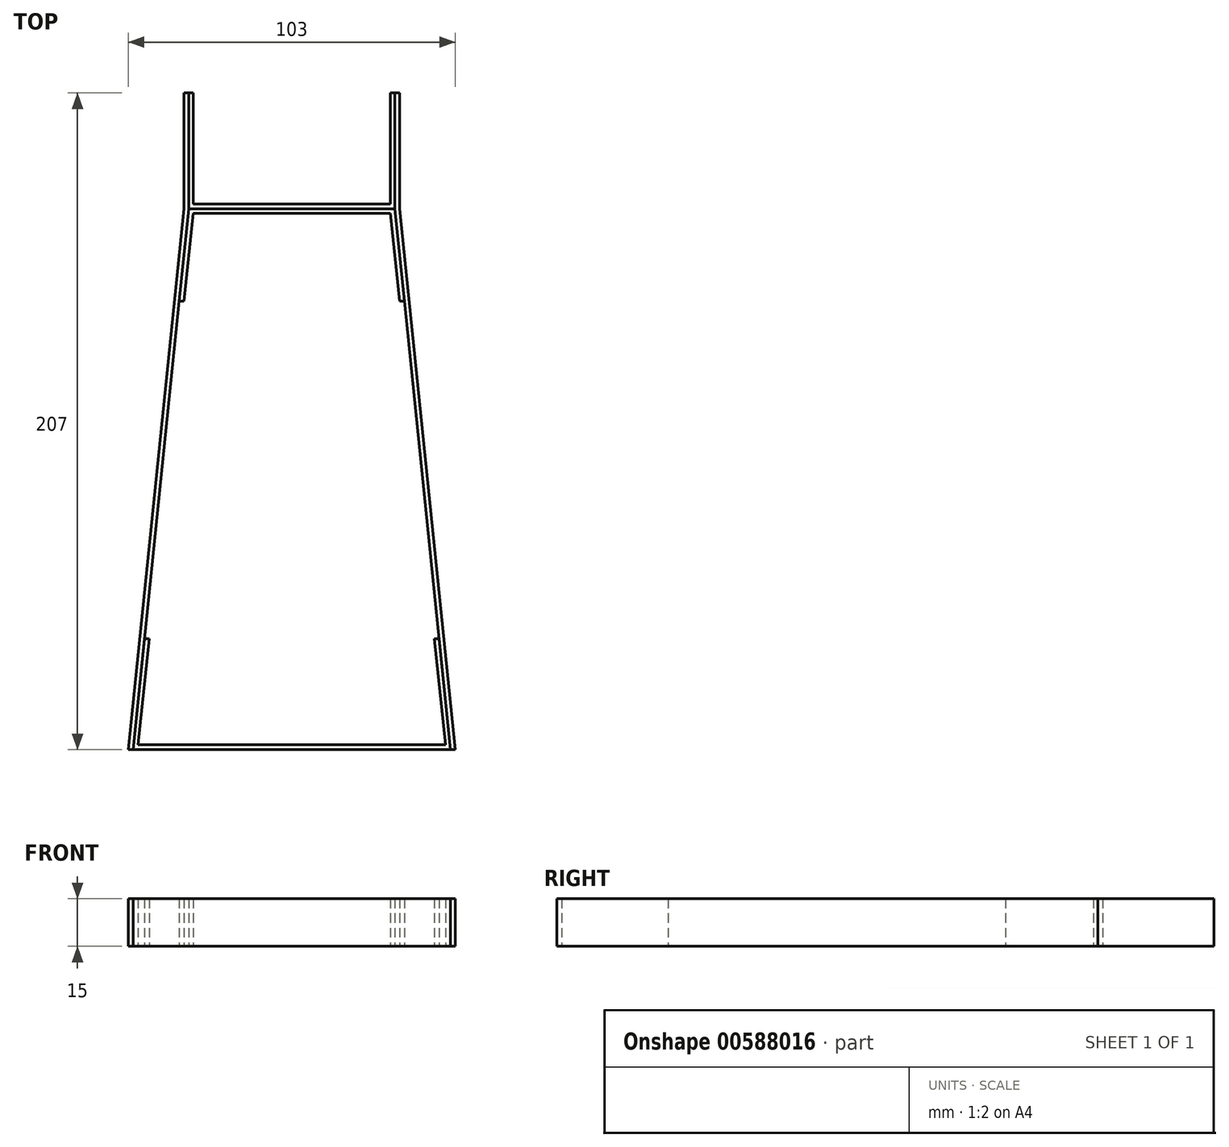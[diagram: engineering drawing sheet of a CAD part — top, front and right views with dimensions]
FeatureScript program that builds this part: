
annotation { "Feature Type Name" : "Feature", "Feature Type Description" : "" }
export const myFeature = defineFeature(function(context is Context, id is Id, definition is map)
    precondition{}
    {
        {
            var Q0;
            Q0=qCreatedBy(makeId("Top.planeOp"),FACE);
            var sketch = newSketch(context, id + "F0", { "sketchPlane" : qUnion([Q0])});
            skLineSegment(sketch, "E0", {"start": v(0, 0) * mm, "end": v(-32.5, 0) * mm});
            skLineSegment(sketch, "E1", {"start": v(-32.5, 0) * mm, "end": v(-32.5, 36.5) * mm});
            skLineSegment(sketch, "E2", {"start": v(-32.5, 36.5) * mm, "end": v(-31, 36.5) * mm});
            skLineSegment(sketch, "E3", {"start": v(-31, 36.5) * mm, "end": v(-31, 1.5) * mm});
            skLineSegment(sketch, "E4", {"start": v(-31, 1.5) * mm, "end": v(0, 1.5) * mm});
            skLineSegment(sketch, "E5.MirrorCS", {"start": v(32.5, 36.5) * mm, "end": v(31, 36.5) * mm});
            skLineSegment(sketch, "E6.MirrorCS", {"start": v(0, 0) * mm, "end": v(32.5, 0) * mm});
            skLineSegment(sketch, "E7.MirrorCS", {"start": v(31, 1.5) * mm, "end": v(0, 1.5) * mm});
            skLineSegment(sketch, "E8.MirrorCS", {"start": v(31, 36.5) * mm, "end": v(31, 1.5) * mm});
            skLineSegment(sketch, "E9.MirrorCS", {"start": v(32.5, 0) * mm, "end": v(32.5, 36.5) * mm});
            skLineSegment(sketch, "E10", {"start": v(-32.5, 0) * mm, "end": v(-35.5, -29.13) * mm});
            skLineSegment(sketch, "E11", {"start": v(-35.5, -29.13) * mm, "end": v(-34, -29.13) * mm});
            skLineSegment(sketch, "E12", {"start": v(-34, -29.13) * mm, "end": v(-31, -1.5) * mm});
            skLineSegment(sketch, "E13", {"start": v(-31, -1.5) * mm, "end": v(0, -1.5) * mm});
            skLineSegment(sketch, "E14.MirrorCS", {"start": v(35.5, -29.13) * mm, "end": v(34, -29.13) * mm});
            skLineSegment(sketch, "E15.MirrorCS", {"start": v(31, -1.5) * mm, "end": v(0, -1.5) * mm});
            skLineSegment(sketch, "E16.MirrorCS", {"start": v(34, -29.13) * mm, "end": v(31, -1.5) * mm});
            skLineSegment(sketch, "E17.MirrorCS", {"start": v(32.5, 0) * mm, "end": v(35.5, -29.13) * mm});
            skLineSegment(sketch, "E18", {"start": v(-34, -29.13) * mm, "end": v(34, -29.13) * mm, "construction": true});
            skLineSegment(sketch, "E19", {"start": v(0, -169) * mm, "end": v(-48.5, -169) * mm});
            skLineSegment(sketch, "E20", {"start": v(-48.5, -169) * mm, "end": v(-44.9, -135.5) * mm});
            skLineSegment(sketch, "E21", {"start": v(-44.9, -135.5) * mm, "end": v(-46.4, -135.5) * mm});
            skLineSegment(sketch, "E22", {"start": v(-46.4, -135.5) * mm, "end": v(-50, -170.5) * mm});
            skLineSegment(sketch, "E23", {"start": v(-50, -170.5) * mm, "end": v(0, -170.5) * mm});
            skLineSegment(sketch, "E24.MirrorCS", {"start": v(44.9, -135.5) * mm, "end": v(46.4, -135.5) * mm});
            skLineSegment(sketch, "E25.MirrorCS", {"start": v(0, -169) * mm, "end": v(48.5, -169) * mm});
            skLineSegment(sketch, "E26.MirrorCS", {"start": v(50, -170.5) * mm, "end": v(0, -170.5) * mm});
            skLineSegment(sketch, "E27.MirrorCS", {"start": v(48.5, -169) * mm, "end": v(44.9, -135.5) * mm});
            skLineSegment(sketch, "E28.MirrorCS", {"start": v(46.4, -135.5) * mm, "end": v(50, -170.5) * mm});
            skLineSegment(sketch, "E29", {"start": v(-32.5, 36.5) * mm, "end": v(-34, 36.5) * mm});
            skLineSegment(sketch, "E30", {"start": v(-34, 36.5) * mm, "end": v(-34, 0) * mm});
            skLineSegment(sketch, "E31", {"start": v(-51.5, -170.5) * mm, "end": v(-50, -170.5) * mm});
            skLineSegment(sketch, "E32", {"start": v(-50, -170.5) * mm, "end": v(-32.5, 0) * mm});
            skLineSegment(sketch, "E33", {"start": v(-34, 0) * mm, "end": v(-51.5, -170.5) * mm});
            skLineSegment(sketch, "E34.MirrorCS", {"start": v(32.5, 36.5) * mm, "end": v(34, 36.5) * mm});
            skLineSegment(sketch, "E35.MirrorCS", {"start": v(34, 36.5) * mm, "end": v(34, 0) * mm});
            skLineSegment(sketch, "E36.MirrorCS", {"start": v(34, 0) * mm, "end": v(51.5, -170.5) * mm});
            skLineSegment(sketch, "E37.MirrorCS", {"start": v(50, -170.5) * mm, "end": v(32.5, 0) * mm});
            skLineSegment(sketch, "E38.MirrorCS", {"start": v(51.5, -170.5) * mm, "end": v(50, -170.5) * mm});
            skSolve(sketch);
        }
        {
            var Q0;
            Q0=makeQuery(id+"F0.imprint","IMPRINT",FACE,{"disambiguationData":[TD([[makeQuery(id+"F0.imprint","IMPRINT",EDGE,{"derivedFrom":sQuery(id+"F0.wireOp",EDGE,"E19")}),1.0]])]});
            extrude(context, id + "F1", {"entities" : qUnion([Q0]), "depth" : 15 * mm, "offsetDistance" : 25 * mm});
        }
        {
            var Q0;
            Q0=makeQuery(id+"F0.imprint","IMPRINT",FACE,{"disambiguationData":[TD([[makeQuery(id+"F0.imprint","IMPRINT",EDGE,{"derivedFrom":sQuery(id+"F0.wireOp",EDGE,"E0")}),-1.0]])]});
            extrude(context, id + "F2", {"entities" : qUnion([Q0]), "depth" : 15 * mm, "offsetDistance" : 25 * mm});
        }
        {
            var Q0;
            {var subQ1=sQuery(id+"F0.wireOp",EDGE,"E0");Q0=makeQuery(id+"F0.imprint","IMPRINT",FACE,{"disambiguationData":[TD([[makeQuery(id+"F0.imprint","IMPRINT",EDGE,{"derivedFrom":subQ1}),1.0]])]});}
            extrude(context, id + "F3", {"entities" : qUnion([Q0]), "depth" : 15 * mm, "offsetDistance" : 25 * mm});
        }
        {
            var Q0;
            Q0=makeQuery(id+"F0.imprint","IMPRINT",FACE,{"disambiguationData":[TD([[makeQuery(id+"F0.imprint","IMPRINT",EDGE,{"derivedFrom":sQuery(id+"F0.wireOp",EDGE,"E1")}),1.0]])]});
            extrude(context, id + "F4", {"entities" : qUnion([Q0]), "depth" : 15 * mm, "offsetDistance" : 25 * mm});
        }
        {
            var Q0;
            {var subQ0=sQuery(id+"F0.wireOp",EDGE,"E17.MirrorCS");Q0=makeQuery(id+"F0.imprint","IMPRINT",FACE,{"disambiguationData":[TD([[makeQuery(id+"F0.imprint","IMPRINT",EDGE,{"derivedFrom":subQ0}),1.0]])]});}
            extrude(context, id + "F5", {"entities" : qUnion([Q0]), "depth" : 15 * mm, "offsetDistance" : 25 * mm});
        }
    });
